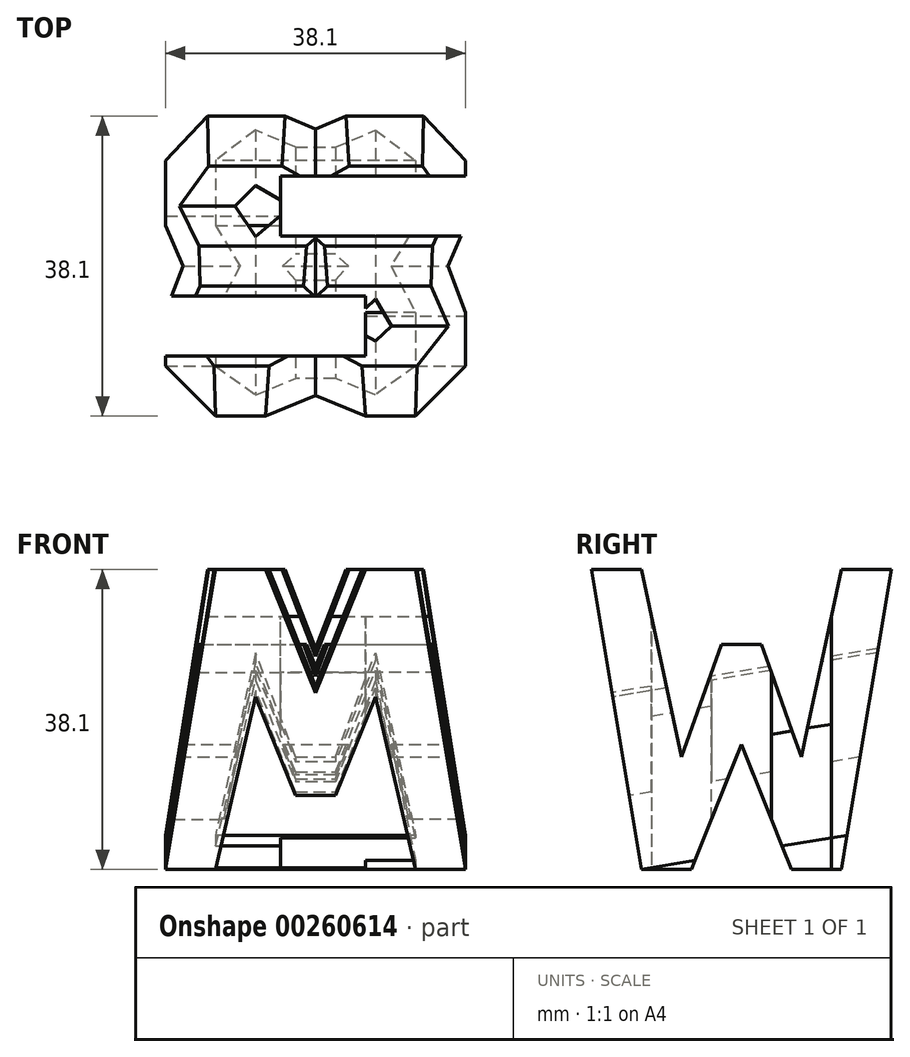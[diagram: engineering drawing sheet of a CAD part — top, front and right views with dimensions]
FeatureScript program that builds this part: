
annotation { "Feature Type Name" : "Feature", "Feature Type Description" : "" }
export const myFeature = defineFeature(function(context is Context, id is Id, definition is map)
    precondition{}
    {
        {
            var Q0;
            Q0=qCreatedBy(makeId("Front.planeOp"),FACE);
            var sketch = newSketch(context, id + "F0", { "sketchPlane" : qUnion([Q0])});
            skLineSegment(sketch, "E0", {"start": v(0, 0) * mm, "end": v(0, 38.1) * mm});
            skLineSegment(sketch, "E1", {"start": v(0, 38.1) * mm, "end": v(38.1, 38.1) * mm});
            skLineSegment(sketch, "E2", {"start": v(38.1, 38.1) * mm, "end": v(38.1, 0) * mm});
            skLineSegment(sketch, "E3", {"start": v(38.1, 0) * mm, "end": v(0, 0) * mm});
            skSolve(sketch);
        }
        {
            var Q0;
            Q0 = qSketchRegion(id + "F0", true);
            extrude(context, id + "F1", {"entities" : qUnion([Q0]), "depth" : 38.1 * mm});
        }
        {
            var Q0;
            Q0=qCreatedBy(makeId("Top.planeOp"),FACE);
            cPlane(context, id + "F2", {"entities" : qUnion([Q0]), "cplaneType" : CPlaneType.OFFSET, "offset" : 38.1 * mm, "width" : 152.4 * mm, "height" : 152.4 * mm});
        }
        {
            var Q0;
            Q0=makeQuery(id+"F1.opExtrude","SWEPT_FACE",FACE,{"disambiguationData":[OSD([sQuery(id+"F0.wireOp",EDGE,"E2")])]});
            var sketch = newSketch(context, id + "F3", { "sketchPlane" : qUnion([Q0])});
            skLineSegment(sketch, "E4", {"start": v(-38.1, 38.1) * mm, "end": v(-31.75, 38.1) * mm});
            skLineSegment(sketch, "E5", {"start": v(0, 38.1) * mm, "end": v(0, 0) * mm});
            skLineSegment(sketch, "E6", {"start": v(0, 0) * mm, "end": v(-38.1, 0) * mm});
            skLineSegment(sketch, "E7", {"start": v(-38.1, 0) * mm, "end": v(-38.1, 38.1) * mm});
            skLineSegment(sketch, "E8", {"start": v(-38.1, 38.1) * mm, "end": v(-31.75, 0) * mm});
            skLineSegment(sketch, "E9", {"start": v(-31.75, 0) * mm, "end": v(-25.4, 0) * mm});
            skLineSegment(sketch, "E10", {"start": v(-25.4, 0) * mm, "end": v(-19.05, 15.88) * mm});
            skLineSegment(sketch, "E11", {"start": v(-19.05, 15.88) * mm, "end": v(-12.7, 0) * mm});
            skLineSegment(sketch, "E12", {"start": v(-12.7, 0) * mm, "end": v(-6.35, 0) * mm});
            skLineSegment(sketch, "E13", {"start": v(-6.35, 0) * mm, "end": v(0, 38.1) * mm});
            skLineSegment(sketch, "E14", {"start": v(-26.67, 14.27) * mm, "end": v(-31.75, 38.1) * mm});
            skLineSegment(sketch, "E15", {"start": v(-6.35, 38.1) * mm, "end": v(0, 38.1) * mm});
            skPoint(sketch, "E16.start.orphan", {"position": v(-12.7, 23.57) * mm});
            skPoint(sketch, "E17.start.orphan", {"position": v(-25.4, 23.57) * mm});
            skLineSegment(sketch, "E18", {"start": v(-26.67, 14.27) * mm, "end": v(-21.59, 28.58) * mm});
            skLineSegment(sketch, "E19", {"start": v(-21.59, 28.58) * mm, "end": v(-16.5, 28.58) * mm});
            skLineSegment(sketch, "E20", {"start": v(-16.5, 28.58) * mm, "end": v(-11.43, 14.27) * mm});
            skLineSegment(sketch, "E21", {"start": v(-11.43, 14.27) * mm, "end": v(-6.35, 38.1) * mm});
            skSolve(sketch);
        }
        {
            var Q0;
            {var subQ0=sQuery(id+"F3.wireOp",EDGE,"E14");Q0=makeQuery(id+"F3.imprint","IMPRINT",FACE,{"disambiguationData":[TD([[makeQuery(id+"F3.imprint","IMPRINT",EDGE,{"derivedFrom":subQ0}),-1.0]])]});}
            var Q1;
            {var subQ0=sQuery(id+"F3.wireOp",EDGE,"E7");Q1=makeQuery(id+"F3.imprint","IMPRINT",FACE,{"disambiguationData":[TD([[makeQuery(id+"F3.imprint","IMPRINT",EDGE,{"derivedFrom":subQ0}),1.0]])]});}
            var Q2;
            {var subQ0=sQuery(id+"F3.wireOp",EDGE,"E10");Q2=makeQuery(id+"F3.imprint","IMPRINT",FACE,{"disambiguationData":[TD([[makeQuery(id+"F3.imprint","IMPRINT",EDGE,{"derivedFrom":subQ0}),-1.0]])]});}
            var Q3;
            {var subQ0=sQuery(id+"F3.wireOp",EDGE,"E5");Q3=makeQuery(id+"F3.imprint","IMPRINT",FACE,{"disambiguationData":[TD([[makeQuery(id+"F3.imprint","IMPRINT",EDGE,{"derivedFrom":subQ0}),-1.0]])]});}
            extrude(context, id + "F4", {"entities" : qUnion([Q0, Q1, Q2, Q3]), "operationType" : NewBodyOperationType.REMOVE, "oppositeDirection" : true, "depth" : 38.1 * mm});
        }
        {
            var Q0;
            Q0=makeQuery(id+"F4.boolean.opBoolean","COPY",FACE,{"derivedFrom":makeQuery(id+"F4.opExtrude","SWEPT_FACE",FACE,{"disambiguationData":[OSD([sQuery(id+"F3.wireOp",EDGE,"E8")])]})});
            var sketch = newSketch(context, id + "F5", { "sketchPlane" : qUnion([Q0])});
            skLineSegment(sketch, "E22", {"start": v(0, 5.22) * mm, "end": v(6.35, 43.85) * mm});
            skLineSegment(sketch, "E23", {"start": v(6.35, 43.85) * mm, "end": v(12.7, 43.85) * mm});
            skLineSegment(sketch, "E24", {"start": v(12.7, 43.85) * mm, "end": v(19.05, 27.97) * mm});
            skLineSegment(sketch, "E25", {"start": v(19.05, 27.97) * mm, "end": v(25.4, 43.85) * mm});
            skLineSegment(sketch, "E26", {"start": v(25.4, 43.85) * mm, "end": v(31.75, 43.85) * mm});
            skLineSegment(sketch, "E27", {"start": v(31.75, 43.85) * mm, "end": v(38.1, 5.22) * mm});
            skLineSegment(sketch, "E28", {"start": v(38.1, 5.22) * mm, "end": v(31.75, 5.22) * mm});
            skLineSegment(sketch, "E29", {"start": v(6.35, 5.22) * mm, "end": v(0, 5.22) * mm});
            skPoint(sketch, "E30.end.orphan", {"position": v(11.43, 27.97) * mm});
            skPoint(sketch, "E31.end.orphan", {"position": v(16.51, 9.35) * mm});
            skPoint(sketch, "E32.end.orphan", {"position": v(20.32, 6) * mm});
            skPoint(sketch, "E33.end.orphan", {"position": v(25.4, 27.97) * mm});
            skLineSegment(sketch, "E34", {"start": v(6.35, 5.22) * mm, "end": v(11.43, 27.44) * mm});
            skLineSegment(sketch, "E35", {"start": v(11.43, 27.44) * mm, "end": v(16.51, 14.74) * mm});
            skLineSegment(sketch, "E36", {"start": v(31.75, 5.22) * mm, "end": v(26.67, 27.44) * mm});
            skLineSegment(sketch, "E37", {"start": v(26.67, 27.44) * mm, "end": v(21.6, 14.74) * mm});
            skLineSegment(sketch, "E38", {"start": v(21.6, 14.74) * mm, "end": v(16.51, 14.74) * mm});
            skSolve(sketch);
        }
        {
            var Q0;
            {var subQ1=sQuery(id+"F5.wireOp",EDGE,"E34");Q0=makeQuery(id+"F5.imprint","IMPRINT",FACE,{"disambiguationData":[TD([[makeQuery(id+"F5.imprint","IMPRINT",EDGE,{"derivedFrom":subQ1}),-1.0]])]});}
            var Q1;
            {var subQ0=sQuery(id+"F5.wireOp",EDGE,"E24");Q1=makeQuery(id+"F5.imprint","IMPRINT",FACE,{"disambiguationData":[TD([[makeQuery(id+"F5.imprint","IMPRINT",EDGE,{"derivedFrom":subQ0}),1.0]])]});}
            var Q2;
            {var subQ0=sQuery(id+"F5.wireOp",EDGE,"E22");Q2=makeQuery(id+"F5.imprint","IMPRINT",FACE,{"disambiguationData":[TD([[makeQuery(id+"F5.imprint","IMPRINT",EDGE,{"derivedFrom":subQ0}),1.0]])]});}
            var Q3;
            {var subQ0=sQuery(id+"F5.wireOp",EDGE,"E27");Q3=makeQuery(id+"F5.imprint","IMPRINT",FACE,{"disambiguationData":[TD([[makeQuery(id+"F5.imprint","IMPRINT",EDGE,{"derivedFrom":subQ0}),1.0]])]});}
            extrude(context, id + "F6", {"entities" : qUnion([Q0, Q1, Q2, Q3]), "operationType" : NewBodyOperationType.REMOVE, "oppositeDirection" : true, "depth" : 38.1 * mm});
        }
        {
            var Q0;
            Q0=qCreatedBy(id+"F2.planeOp",FACE);
            var sketch = newSketch(context, id + "F7", { "sketchPlane" : qUnion([Q0])});
            skLineSegment(sketch, "E39", {"start": v(0, 0) * mm, "end": v(38.1, 0) * mm});
            skLineSegment(sketch, "E40", {"start": v(38.1, 0) * mm, "end": v(38.1, -38.1) * mm});
            skLineSegment(sketch, "E41", {"start": v(38.1, -38.1) * mm, "end": v(0, -38.1) * mm});
            skLineSegment(sketch, "E42", {"start": v(0, -38.1) * mm, "end": v(0, 0) * mm});
            skLineSegment(sketch, "E43", {"start": v(38.1, -7.62) * mm, "end": v(14.63, -7.62) * mm});
            skLineSegment(sketch, "E44", {"start": v(14.63, -7.62) * mm, "end": v(14.63, -15.24) * mm});
            skLineSegment(sketch, "E45", {"start": v(14.63, -15.24) * mm, "end": v(38.1, -15.24) * mm});
            skLineSegment(sketch, "E46", {"start": v(38.1, -15.24) * mm, "end": v(38.1, -7.62) * mm});
            skLineSegment(sketch, "E47", {"start": v(0, -30.48) * mm, "end": v(25.4, -30.48) * mm});
            skLineSegment(sketch, "E48", {"start": v(25.4, -30.48) * mm, "end": v(25.4, -22.86) * mm});
            skLineSegment(sketch, "E49", {"start": v(25.4, -22.86) * mm, "end": v(0, -22.86) * mm});
            skLineSegment(sketch, "E50", {"start": v(0, -22.86) * mm, "end": v(0, -30.48) * mm});
            skPoint(sketch, "E51.start.orphan", {"position": v(12.7, -30.48) * mm});
            skPoint(sketch, "E52.end.orphan", {"position": v(30.14, 0) * mm});
            skSolve(sketch);
        }
        {
            var Q0;
            Q0=makeQuery(id+"F7.imprint","IMPRINT",FACE,{"disambiguationData":[TD([[makeQuery(id+"F7.imprint","IMPRINT",EDGE,{"derivedFrom":sQuery(id+"F7.wireOp",EDGE,"E43")}),1.0]])]});
            var Q1;
            Q1=makeQuery(id+"F7.imprint","IMPRINT",FACE,{"disambiguationData":[TD([[makeQuery(id+"F7.imprint","IMPRINT",EDGE,{"derivedFrom":sQuery(id+"F7.wireOp",EDGE,"E47")}),1.0]])]});
            extrude(context, id + "F8", {"entities" : qUnion([Q0, Q1]), "operationType" : NewBodyOperationType.REMOVE, "oppositeDirection" : true, "depth" : 38.1 * mm});
        }
    });
